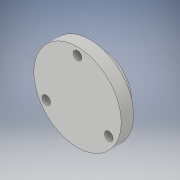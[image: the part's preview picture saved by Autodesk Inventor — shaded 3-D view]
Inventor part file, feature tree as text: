
AUTODESK INVENTOR PART (.ipt)
format: ipt  version: 2018 (Build 220112000, 112)  size: 111,616 bytes
history: native  units: in
note: dims shown in document units (in); Inventor stores cm internally (conversion verified against a paired STEP export)
features: extrude x2, sketch x1, hole x1
ambient origin geometry x8: Origin, YZ Plane, XZ Plane, XY Plane, X Axis, Y Axis, Z Axis, Center Point
bodies: Solid1 (feature_tree)
feature tree (4):
  sketch  "Sketch1"  dims[d0=1.75in d1=1.45in d2=1.1811in d4=360.0deg d6=0.25in d7=0.0in d8=0.172in d9=0.75in d10=0.375in d11=0.25in d12=0.5635in d13=1.0in d14=0.8108in d16=1.165in d17=0.25in d18=0.0in]
  extrude  "Extrusion1"  Depth=0.25in
  hole  "Hole1"  [1 undecoded]
  extrude  "Extrusion2"  Depth=0.25in TaperAngle=0.0deg
note: 1 required parameter value undecoded (feature->parameter linkage not recoverable at this tier; creation-order binding heuristic only, values carry confidence <= 0.55)
